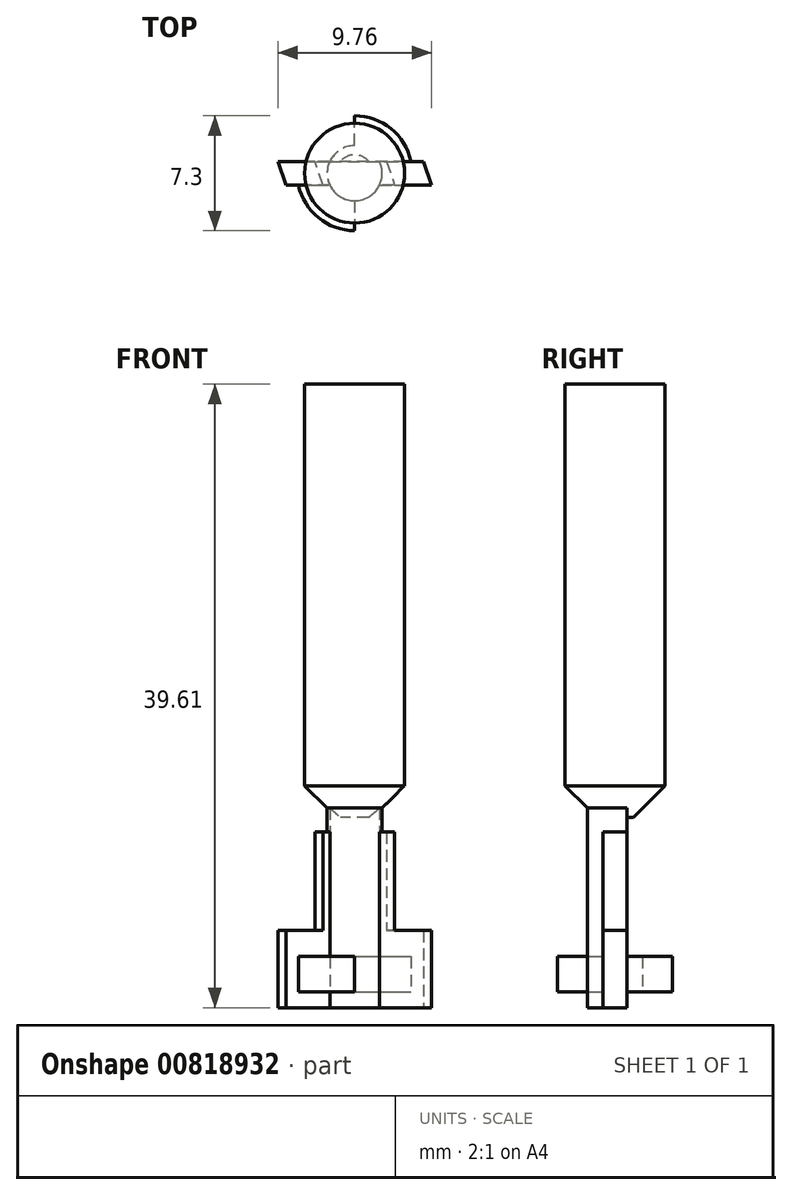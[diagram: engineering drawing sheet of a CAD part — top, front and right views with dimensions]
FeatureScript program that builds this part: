
annotation { "Feature Type Name" : "Feature", "Feature Type Description" : "" }
export const myFeature = defineFeature(function(context is Context, id is Id, definition is map)
    precondition{}
    {
        {
            var Q0;
            Q0=qCreatedBy(makeId("Front.planeOp"),FACE);
            var sketch = newSketch(context, id + "F0", { "sketchPlane" : qUnion([Q0])});
            skLineSegment(sketch, "E0.bottom", {"start": v(4.88, -8.04) * mm, "end": v(-4.87, -8.04) * mm});
            skLineSegment(sketch, "E0.left", {"start": v(4.87, -8.04) * mm, "end": v(4.87, -3.12) * mm});
            skLineSegment(sketch, "E0.right", {"start": v(-4.88, -8.04) * mm, "end": v(-4.88, -3.13) * mm});
            skPoint(sketch, "E0.middle", {"position": v(0, 0) * mm});
            skLineSegment(sketch, "E1", {"start": v(-4.88, -3.13) * mm, "end": v(-2.52, -3.13) * mm});
            skLineSegment(sketch, "E2.top", {"start": v(2.52, 3.13) * mm, "end": v(-2.53, 3.12) * mm});
            skLineSegment(sketch, "E2.left", {"start": v(2.53, -3.12) * mm, "end": v(2.52, 3.13) * mm});
            skLineSegment(sketch, "E2.right", {"start": v(-2.52, -3.13) * mm, "end": v(-2.53, 3.12) * mm});
            skPoint(sketch, "E0.top.start.orphan", {"position": v(4.87, 8.04) * mm});
            skPoint(sketch, "E3.orphan", {"position": v(-4.88, 8.03) * mm});
            skLineSegment(sketch, "E4.trimOffspring", {"start": v(2.53, -3.12) * mm, "end": v(4.87, -3.12) * mm});
            skLineSegment(sketch, "E5", {"start": v(0, -14.74) * mm, "end": v(0, 18.34) * mm, "construction": true});
            skSolve(sketch);
        }
        {
            var Q0;
            Q0=makeQuery(id+"F0.imprint","IMPRINT",FACE,{"disambiguationData":[TD([[makeQuery(id+"F0.imprint","IMPRINT",EDGE,{"derivedFrom":sQuery(id+"F0.wireOp",EDGE,"E0.bottom")}),-1.0]])]});
            extrude(context, id + "F1", {"entities" : qUnion([Q0]), "endBound" : BoundingType.SYMMETRIC, "depth" : 1.5 * mm, "offsetDistance" : 25 * mm});
        }
        {
            var Q0;
            Q0=makeQuery(id+"F1.opExtrude","CAP_EDGE",EDGE,{"disambiguationData":[OSD([sQuery(id+"F0.wireOp",EDGE,"E0.right")])],"isStart":false});
            var Q1;
            Q1=makeQuery(id+"F1.opExtrude","CAP_EDGE",EDGE,{"disambiguationData":[OSD([sQuery(id+"F0.wireOp",EDGE,"E2.right")])],"isStart":false});
            var Q2;
            Q2=makeQuery(id+"F1.opExtrude","CAP_EDGE",EDGE,{"disambiguationData":[OSD([sQuery(id+"F0.wireOp",EDGE,"E2.left")])],"isStart":true});
            var Q3;
            Q3=makeQuery(id+"F1.opExtrude","CAP_EDGE",EDGE,{"disambiguationData":[OSD([sQuery(id+"F0.wireOp",EDGE,"E0.left")])],"isStart":true});
            chamfer(context, id + "F2", {"entities" : qUnion([Q0, Q1, Q2, Q3]), "chamferType" : ChamferType.TWO_OFFSETS, "width1" : 1.5 * mm, "oppositeDirection" : false, "width2" : .5 * mm, "tangentPropagation" : true});
        }
        {
            var Q0;
            Q0=makeQuery(id+"F1.opExtrude","SWEPT_FACE",FACE,{"disambiguationData":[OSD([sQuery(id+"F0.wireOp",EDGE,"E0.bottom")])]});
            var sketch = newSketch(context, id + "F3", { "sketchPlane" : qUnion([Q0])});
            skCircle(sketch, "E6", {"center": v(0, 0) * mm, "radius": 1.75 * mm});
            skSolve(sketch);
        }
        {
            var Q0;
            {var subQ0=sQuery(id+"F3.wireOp",EDGE,"E6");var subQ1=makeQuery(id+"F1.opExtrude","CAP_EDGE",EDGE,{"disambiguationData":[OSD([sQuery(id+"F0.wireOp",EDGE,"E0.bottom")])],"isStart":true});var subQ2=makeQuery(id+"F3.imprint","INTERSECT",VERTEX,{"disambiguationData":[OD(0.0)],"derivedFrom":[subQ1,subQ0]});Q0=makeQuery(id+"F3.imprint","IMPRINT",FACE,{"disambiguationData":[TD([[makeQuery(id+"F3.imprint","IMPRINT",EDGE,{"disambiguationData":[TD([[subQ2,-1.0]])],"derivedFrom":subQ0}),1.0]])]});}
            var Q1;
            {var subQ0=sQuery(id+"F3.wireOp",EDGE,"E6");var subQ1=makeQuery(id+"F1.opExtrude","CAP_EDGE",EDGE,{"disambiguationData":[OSD([sQuery(id+"F0.wireOp",EDGE,"E0.bottom")])],"isStart":false});var subQ2=makeQuery(id+"F3.imprint","INTERSECT",VERTEX,{"disambiguationData":[OD(0.0)],"derivedFrom":[subQ1,subQ0]});Q1=makeQuery(id+"F3.imprint","IMPRINT",FACE,{"disambiguationData":[TD([[makeQuery(id+"F3.imprint","IMPRINT",EDGE,{"disambiguationData":[TD([[subQ2,1.0]])],"derivedFrom":subQ0}),1.0]])]});}
            var Q2;
            {var subQ0=sQuery(id+"F3.wireOp",EDGE,"E6");var subQ1=sQuery(id+"F0.wireOp",EDGE,"E0.bottom");var subQ2=makeQuery(id+"F1.opExtrude","CAP_EDGE",EDGE,{"disambiguationData":[OSD([subQ1])],"isStart":false});var subQ3=makeQuery(id+"F3.imprint","INTERSECT",VERTEX,{"disambiguationData":[OD(0.0)],"derivedFrom":[subQ2,subQ0]});Q2=makeQuery(id+"F3.imprint","IMPRINT",FACE,{"disambiguationData":[TD([[makeQuery(id+"F3.imprint","IMPRINT",EDGE,{"disambiguationData":[TD([[subQ3,-1.0]])],"derivedFrom":subQ0}),1.0]])]});}
            extrude(context, id + "F4", {"entities" : qUnion([Q0, Q1, Q2]), "operationType" : NewBodyOperationType.ADD, "oppositeDirection" : true, "depth" : 12.1 * mm, "offsetDistance" : 25 * mm});
        }
        {
            var Q0;
            Q0=makeQuery(id+"F4.opExtrude","CAP_FACE",FACE,{"disambiguationData":[OSD([sQuery(id+"F3.wireOp",EDGE,"E6")])],"isStart":false});
            var sketch = newSketch(context, id + "F5", { "sketchPlane" : qUnion([Q0])});
            skCircle(sketch, "E7", {"center": v(0, 0) * mm, "radius": 3.17 * mm});
            skSolve(sketch);
        }
        {
            var Q0;
            Q0 = qSketchRegion(id + "F5", true);
            extrude(context, id + "F6", {"entities" : qUnion([Q0]), "operationType" : NewBodyOperationType.ADD, "depth" : 27.5 * mm, "offsetDistance" : 25 * mm});
        }
        {
            var Q0;
            Q0=makeQuery(id+"F6.opExtrude","CAP_EDGE",EDGE,{"disambiguationData":[OSD([sQuery(id+"F5.wireOp",EDGE,"E7")])],"isStart":true});
            chamfer(context, id + "F7", {"entities" : qUnion([Q0]), "width" : 2 * mm, "tangentPropagation" : true});
        }
        {
            var Q0;
            Q0=makeQuery(id+"F4.boolean.opBoolean","MERGE",FACE,{"derivedFrom":[makeQuery(id+"F1.opExtrude","SWEPT_FACE",FACE,{"disambiguationData":[OSD([sQuery(id+"F0.wireOp",EDGE,"E0.bottom")])]}),makeQuery(id+"F4.opExtrude","CAP_FACE",FACE,{"disambiguationData":[OSD([sQuery(id+"F3.wireOp",EDGE,"E6")])],"isStart":true})]});
            cPlane(context, id + "F8", {"entities" : qUnion([Q0]), "cplaneType" : CPlaneType.OFFSET, "offset" : 1 * mm, "oppositeDirection" : true, "width" : 150 * mm, "height" : 150 * mm});
        }
        {
            var Q0;
            Q0=qCreatedBy(id+"F8.planeOp",FACE);
            var sketch = newSketch(context, id + "F9", { "sketchPlane" : qUnion([Q0])});
            skCircle(sketch, "E8", {"center": v(0, 0) * mm, "radius": 3.65 * mm});
            skSolve(sketch);
        }
        {
            var Q0;
            Q0 = qSketchRegion(id + "F9", true);
            extrude(context, id + "F10", {"entities" : qUnion([Q0]), "operationType" : NewBodyOperationType.ADD, "oppositeDirection" : true, "depth" : 2.25 * mm, "offsetDistance" : 25 * mm});
        }
        {
            var Q0;
            Q0=qCreatedBy(id+"F8.planeOp",FACE);
            var sketch = newSketch(context, id + "F11", { "sketchPlane" : qUnion([Q0])});
            skLineSegment(sketch, "E9.left", {"start": v(0, -1.75) * mm, "end": v(0, -4.02) * mm});
            skPoint(sketch, "E10.orphan", {"position": v(0, 0.75) * mm});
            skLineSegment(sketch, "E11.trimOffspring", {"start": v(0, 1.75) * mm, "end": v(0, 4.92) * mm});
            skLineSegment(sketch, "E12.MirrorCS", {"start": v(0, 4.92) * mm, "end": v(5.58, 4.92) * mm});
            skLineSegment(sketch, "E13.MirrorCS", {"start": v(5.58, 0.75) * mm, "end": v(5.58, 4.92) * mm});
            skLineSegment(sketch, "E14.MirrorCS", {"start": v(5.58, 0.75) * mm, "end": v(1.58, 0.75) * mm});
            skArc(sketch, "E15.MirrorCS", {"start": v(0, 1.75) * mm, "mid": v(0.93, 1.48) * mm, "end": v(1.58, 0.75) * mm});
            skPoint(sketch, "E16.right.end.orphan", {"position": v(-5.58, 4.92) * mm});
            skPoint(sketch, "E17.start.orphan", {"position": v(-5.58, 0.75) * mm});
            skPoint(sketch, "E18.end.orphan", {"position": v(-1.58, 0.75) * mm});
            skLineSegment(sketch, "E19.MirrorCS", {"start": v(0, -4.02) * mm, "end": v(-4.76, -4.02) * mm});
            skLineSegment(sketch, "E20.MirrorCS", {"start": v(-4.76, -0.75) * mm, "end": v(-4.76, -4.02) * mm});
            skLineSegment(sketch, "E21.MirrorCS", {"start": v(-1.58, -0.75) * mm, "end": v(-4.76, -0.75) * mm});
            skArc(sketch, "E22.MirrorCS", {"start": v(0, -1.75) * mm, "mid": v(-0.93, -1.48) * mm, "end": v(-1.58, -0.75) * mm});
            skPoint(sketch, "E23.start.orphan", {"position": v(1.58, -0.75) * mm});
            skPoint(sketch, "E9.right.start.orphan", {"position": v(4.76, -0.75) * mm});
            skPoint(sketch, "E9.top.end.orphan", {"position": v(4.76, -4.02) * mm});
            skSolve(sketch);
        }
        {
            var Q0;
            Q0 = qSketchRegion(id + "F11", true);
            extrude(context, id + "F12", {"entities" : qUnion([Q0]), "operationType" : NewBodyOperationType.REMOVE, "oppositeDirection" : true, "depth" : 10 * mm, "offsetDistance" : 25 * mm});
        }
    });
